# Revit family: TSM Betonschraube Linsenkopf mit TX-Antrieb, vz
name_source: partatom
category: HLS-Bauteile
units: mm (PartAtom-declared; Revit-internal decimal feet)

## family parameters
Arbeitsebenenbasiert = Ja
Beim Laden mit Abzugskörper schneiden = Nein
Bemaßung runder Anschluss = Durchmesser verwenden
Beschriftungsausrichtung beibehalten = Nein
Gemeinsam genutzt = Ja
Immer vertikal = Nein
Raumberechnungspunkt = Nein
Teiletyp = Normal

## types (2) — shared parameters
Bohrerdurchmesser = 6 mm
Fabrikat = Toge
Firma = MEFA Befestigungs- und Montagesysteme GmbH
Form Kopf = Linsenkopf
Gewicht = 0.01 kg
Gewicht pro Bauteil = 0.01 kg
Material = Stahl
Mengeneinheit = St
Oberflaeche = galvanisch verzinkt
Vorgabe-Ansicht = 1219 mm
vpe = 100

## per-type parameters (varying)
| type | Artikelnummer | Durchmesser Kopf | EAN | Kurztext1 | Kurztext2 | Länge | max. Klemmstärke | min. Bohrlochtiefe | min. Verankerungstiefe |
| TSM Betonschrauben Linsenkopf mit TX-Antrieb, vz  6x 40 Liko | 2230640 | 14.4 mm | 4250928463647 | Betonschraube TSM 6 TX 30 | 6x40 mm Linsenkopf 14,4 mm | 40 mm  [stored 0.131234 ft] | 5 mm  [stored 0.0164042 ft] | 40 mm | 35 mm |
| TSM Betonschrauben Linsenkopf mit TX-Antrieb, vz  6x 28 Liko | 2230628 | 15 mm | 4250928449221 | Betonschraube TSM-L 6 VZ 30 | 6x28 mm Linsenkopf 15 mm | 28 mm  [stored 0.0918635 ft] | 3 mm  [stored 0.00984252 ft] | 28 mm | 25 mm |

note: [stored X ft] marks values corroborated as IEEE doubles in the binary element streams (Revit-internal decimal feet)
